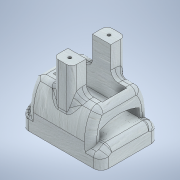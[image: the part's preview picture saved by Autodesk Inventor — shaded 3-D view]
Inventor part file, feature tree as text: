
AUTODESK INVENTOR PART (.ipt)
format: ipt  version: 2021 (Build 250183000, 183)  size: 1,108,992 bytes
history: native  units: mm
features: extrude x20, sketch x20, fillet x7, projected_geometry x7, plane x1, mirror x1
ambient origin geometry x8: Origin, YZ Plane, XZ Plane, XY Plane, X Axis, Y Axis, Z Axis, Center Point
bodies: Solid1 (feature_tree)
feature tree (56):
  extrude  "Extrusion1"  Depth=39.0mm
  extrude  "Extrusion2"  Depth=8.0mm
  plane  "Work Plane2"
  mirror  "Mirror1"
  extrude  "Extrusion3"  Depth=8.0mm
  extrude  "Extrusion4"  Depth=4.0mm TaperAngle=0.0deg
  extrude  "Extrusion5"  Depth=10.0mm
  extrude  "Extrusion6"  Depth=4.0mm TaperAngle=0.0deg
  extrude  "Extrusion7"  Depth=19.0mm
  extrude  "Extrusion8"  Depth=4.0mm TaperAngle=0.0deg
  extrude  "Extrusion9"  Depth=4.0mm TaperAngle=0.0deg
  extrude  "Extrusion10"  Depth=2.0mm TaperAngle=0.0deg
  extrude  "Extrusion11"  Depth=12.5mm
  extrude  "Extrusion12"  Depth=4.0mm
  extrude  "Extrusion13"  Depth=7.9mm
  extrude  "Extrusion14"  Depth=7.9mm
  extrude  "Extrusion15"  Depth=15.0mm TaperAngle=0.0deg
  extrude  "Extrusion16"  Depth=8.5mm TaperAngle=0.0deg
  extrude  "Extrusion17"  Depth=8.5mm TaperAngle=0.0deg
  fillet  "Fillet6"  Radius=36.0mm
  fillet  "Fillet7"  Radius=8.5mm
  fillet  "Fillet8"  Radius=15.0mm
  extrude  "Extrusion18"  Depth=6.0mm
  fillet  "Fillet9"  Radius=6.0mm
  fillet  "Fillet10"  Radius=30.0mm
  extrude  "Extrusion19"  Depth=3.0mm
  fillet  "Fillet12"  Radius=5.0mm
  fillet  "Fillet13"  Radius=5.0mm
  extrude  "Extrusion20"  Depth=3.0mm
  sketch  "Sketch1"  dims[d0=15.0mm d1=39.0mm]
  sketch  "Sketch2"  dims[d2=4.0mm d3=0.0mm d5=8.0mm]
  sketch  "Sketch3"  dims[d6=15.0mm d7=8.0mm]
  sketch  "Sketch4"  dims[d8=14.0mm d9=4.0mm d10=0.0mm]
  sketch  "Sketch5"  dims[d12=10.0mm d13=27.0mm]
  sketch  "Sketch7"  dims[d14=28.0mm d15=4.0mm d16=0.0mm]
  sketch  "Sketch8"  dims[d17=28.0mm d18=19.0mm]
  sketch  "Sketch10"  dims[d19=4.0mm d20=0.0mm d21=4.0mm d22=0.0mm]
  projected_geometry  "Projected Loop2"
  sketch  "Sketch11"  dims[d23=13.0mm d24=0.0mm d25=4.0mm d26=0.0mm]
  projected_geometry  "Projected Loop3"
  sketch  "Sketch12"  dims[d27=3.0mm d28=0.0mm d29=2.0mm d30=0.0mm]
  projected_geometry  "Projected Loop4"
  sketch  "Sketch14"  dims[d31=2.0mm d32=0.0mm d35=12.5mm]
  sketch  "Sketch15"  dims[d36=11.5mm d37=4.0mm]
  sketch  "Sketch18"  dims[d38=6.0mm d39=7.9mm]
  sketch  "Sketch19"  dims[d40=7.9mm d41=7.9mm]
  projected_geometry  "Projected Loop9"
  sketch  "Sketch20"  dims[d42=7.9mm d43=15.0mm d44=0.0mm]
  projected_geometry  "Projected Loop10"
  sketch  "Sketch21"  dims[d45=0.2mm d46=0.0mm d49=8.5mm d50=56.5mm d51=0.0mm d52=0.0mm]
  sketch  "Sketch22"  dims[d53=8.5mm d54=0.0mm d55=8.5mm d56=0.0mm d57=36.0mm d58=8.5mm d59=0.0mm d61=15.0mm d62=0.0mm]
  sketch  "Sketch23"  dims[d63=4.0mm d64=6.0mm d65=6.0mm d66=30.0mm]
  sketch  "Sketch24"  dims[d70=8.5mm d71=0.0mm d72=3.0mm d73=5.0mm d75=5.0mm d76=0.0mm]
  projected_geometry  "Projected Loop11"
  projected_geometry  "Projected Loop12"
  sketch  "Sketch25"  dims[d77=5.0mm d78=3.0mm d79=7.9mm d80=7.9mm d81=7.9mm d82=7.9mm d83=11.0mm d84=11.0mm d85=11.0mm d86=11.0mm d88=11.0mm d89=11.0mm d90=11.0mm d91=11.0mm d92=2.4mm d93=2.4mm d94=15.0mm d95=0.0mm]
